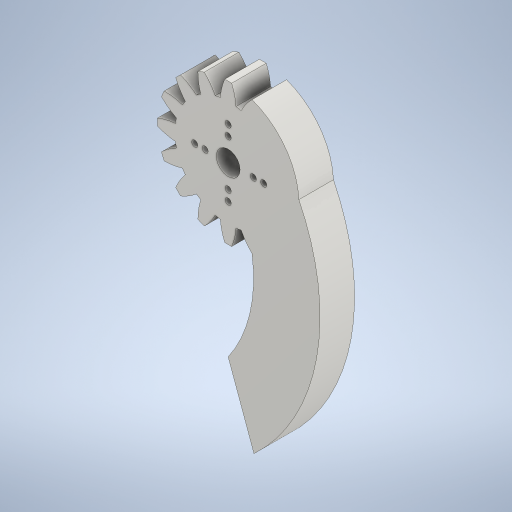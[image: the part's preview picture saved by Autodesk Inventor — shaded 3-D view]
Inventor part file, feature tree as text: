
AUTODESK INVENTOR PART (.ipt)
format: ipt  version: 2024 (Build 280153000, 153)  size: 841,728 bytes
history: native  units: mm (DEFAULTED — no unit token found)
features: other x7, extrude x3, plane x3, sketch x3, reference x1, projected_geometry x1
ambient origin geometry x8: Origin, YZ Plane, XZ Plane, XY Plane, X Axis, Y Axis, Z Axis, Center Point
bodies: Solid1 (feature_tree)
feature tree (18):
  extrude  "Extrusion1"  Depth=6.666667mm TaperAngle=0.0deg
  plane  "Work Plane2"
  plane  "Work Plane8"
  plane  "Work Plane9"
  other  "Spur Gear"
  extrude  "Extrusion2"  Depth=10.0mm TaperAngle=0.0deg
  extrude  "Extrusion3"  TaperAngle=0.0deg  [1 undecoded]
  sketch  "Sketch1"  dims[d0=27.3mm d1=6.666667mm d2=0.0mm]
  other  "Srf1"
  sketch  "Sketch3"  dims[d3=24.0mm d4=10.0mm d5=0.0mm]
  reference  "Reference1"
  sketch  "Sketch4"  dims[d16=23.4mm d17=0.0mm d34=1.963495mm d39=0.0mm d41=0.0mm d43=23.4mm d46=23.4mm d47=0.0mm d48=0.0mm d49=10.0mm d50=0.0mm d51=50.0mm d52=79.653867mm d53=54.037661mm d54=6.666667mm d55=0.0mm d61=3.490659mm]
  projected_geometry  "Projected Loop1"
  other  "Pitch Diameter"
  other  "<userpath> windows\Documents\Inventor\Robotska_roka\roka_asemb.iam"
  other  "roka_asemb.iam"
  other  "SG90 - Micro Servo 9g - Tower Pro:2"
  other  "SG90 - Micro Servo 9g - Tower Pro.4"
note: 1 required parameter value undecoded (feature->parameter linkage not recoverable at this tier; creation-order binding heuristic only, values carry confidence <= 0.55)
